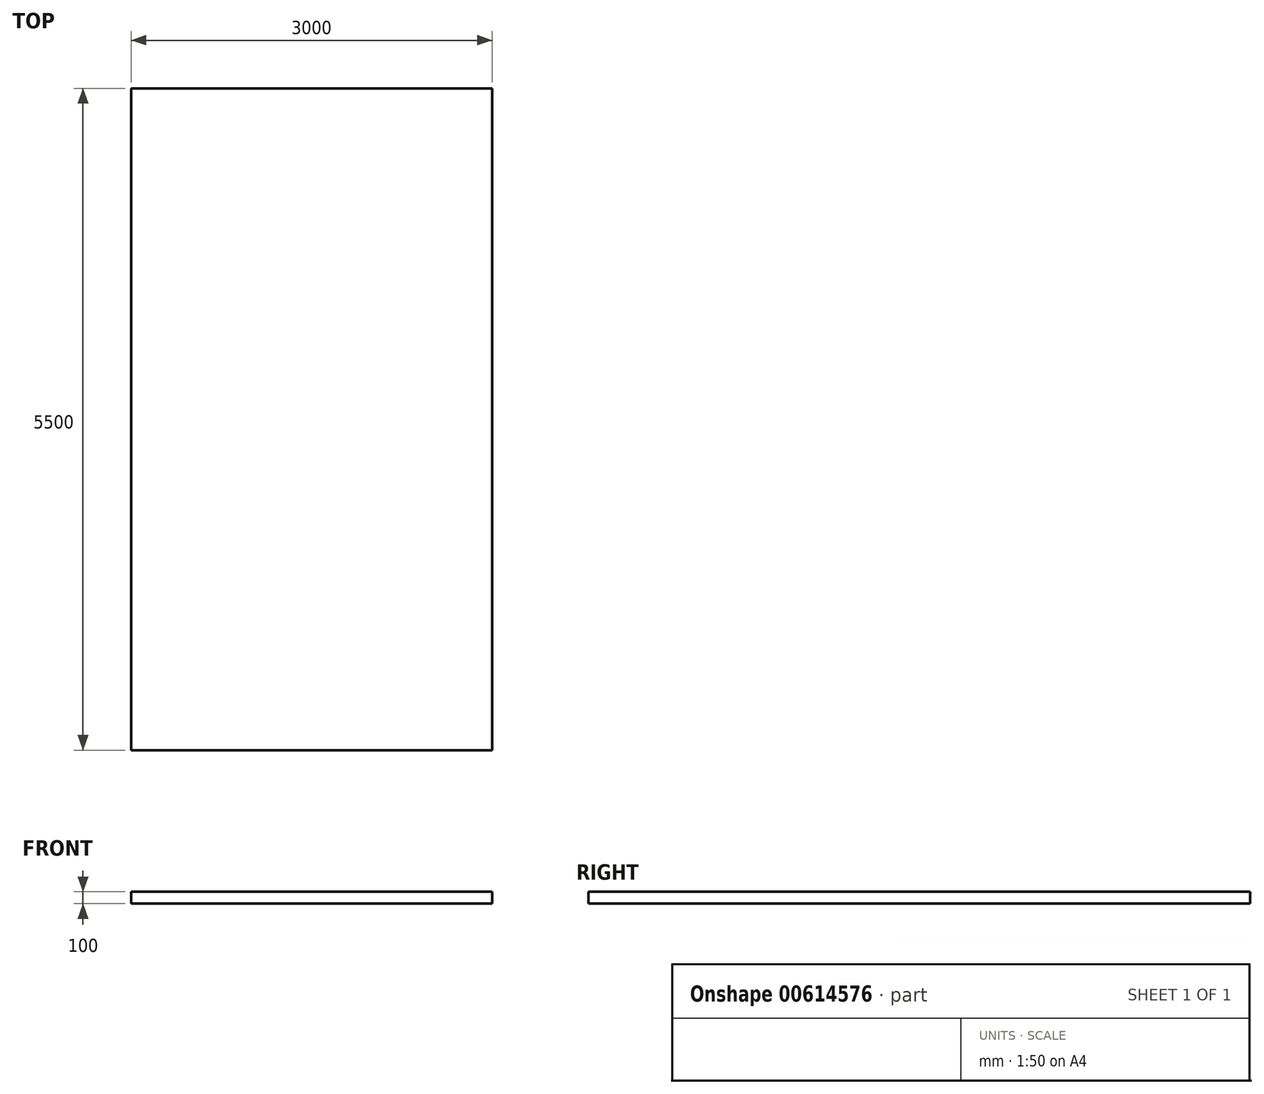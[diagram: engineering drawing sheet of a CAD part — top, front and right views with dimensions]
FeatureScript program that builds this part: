
annotation { "Feature Type Name" : "Feature", "Feature Type Description" : "" }
export const myFeature = defineFeature(function(context is Context, id is Id, definition is map)
    precondition{}
    {
        {
            var Q0;
            Q0=qCreatedBy(makeId("Top.planeOp"),FACE);
            var sketch = newSketch(context, id + "F0", { "sketchPlane" : qUnion([Q0])});
            skLineSegment(sketch, "E0.bottom", {"start": v(1500, 2750) * mm, "end": v(-1500, 2750) * mm});
            skLineSegment(sketch, "E0.top", {"start": v(1500, -2750) * mm, "end": v(-1500, -2750) * mm});
            skLineSegment(sketch, "E0.left", {"start": v(1500, 2750) * mm, "end": v(1500, -2750) * mm});
            skLineSegment(sketch, "E0.right", {"start": v(-1500, 2750) * mm, "end": v(-1500, -2750) * mm});
            skPoint(sketch, "E0.middle", {"position": v(0, 0) * mm});
            skSolve(sketch);
        }
        {
            var Q0;
            Q0=makeQuery(id+"F0.imprint","IMPRINT",FACE,{"disambiguationData":[TD([[makeQuery(id+"F0.imprint","IMPRINT",EDGE,{"derivedFrom":sQuery(id+"F0.wireOp",EDGE,"E0.bottom")}),1.0]])]});
            extrude(context, id + "F1", {"entities" : qUnion([Q0]), "depth" : 100 * mm, "offsetDistance" : 25 * mm});
        }
    });
